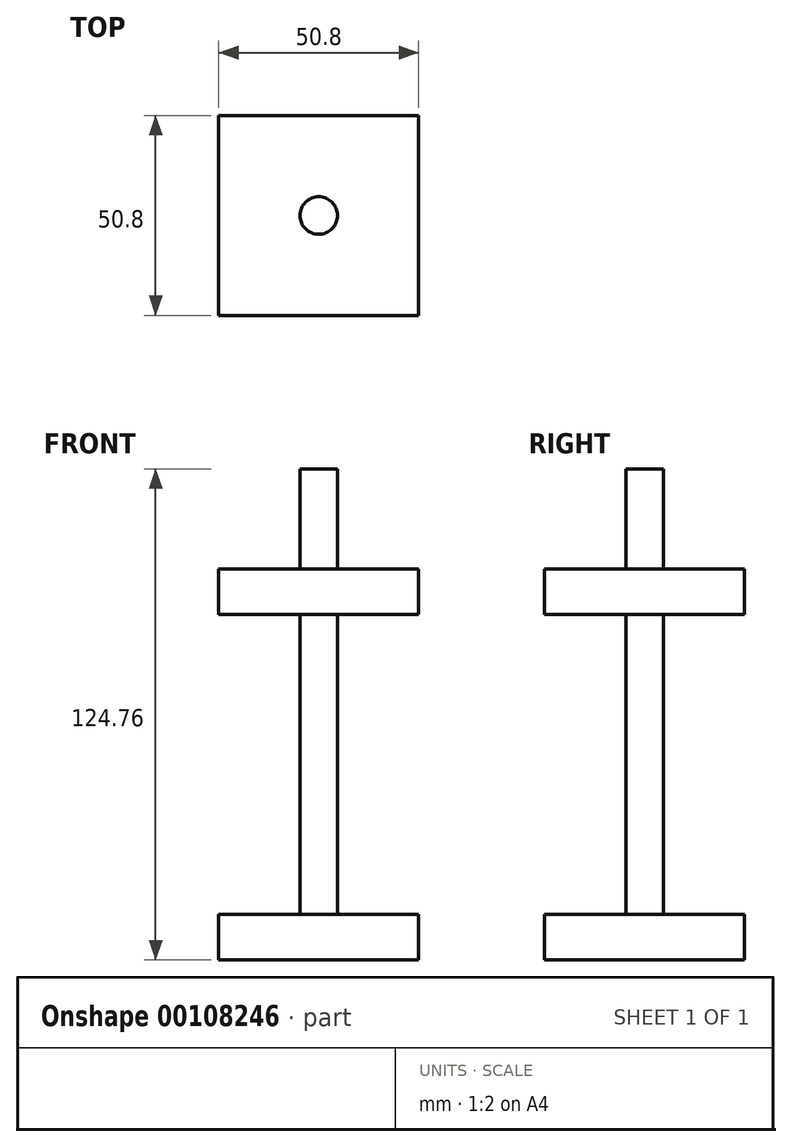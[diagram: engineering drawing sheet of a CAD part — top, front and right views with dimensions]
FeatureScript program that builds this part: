
annotation { "Feature Type Name" : "Feature", "Feature Type Description" : "" }
export const myFeature = defineFeature(function(context is Context, id is Id, definition is map)
    precondition{}
    {
        {
            var Q0;
            Q0=qCreatedBy(makeId("Top.planeOp"),FACE);
            var sketch = newSketch(context, id + "F0", { "sketchPlane" : qUnion([Q0])});
            skLineSegment(sketch, "E0.bottom", {"start": v(25.4, 25.4) * mm, "end": v(-25.4, 25.4) * mm});
            skLineSegment(sketch, "E0.top", {"start": v(25.4, -25.4) * mm, "end": v(-25.4, -25.4) * mm});
            skLineSegment(sketch, "E0.left", {"start": v(25.4, 25.4) * mm, "end": v(25.4, -25.4) * mm});
            skLineSegment(sketch, "E0.right", {"start": v(-25.4, 25.4) * mm, "end": v(-25.4, -25.4) * mm});
            skPoint(sketch, "E0.middle", {"position": v(0, 0) * mm});
            skSolve(sketch);
        }
        {
            var Q0;
            Q0=makeQuery(id+"F0.imprint","IMPRINT",FACE,{"disambiguationData":[TD([[makeQuery(id+"F0.imprint","IMPRINT",EDGE,{"derivedFrom":sQuery(id+"F0.wireOp",EDGE,"E0.bottom")}),1.0]])]});
            extrude(context, id + "F1", {"entities" : qUnion([Q0]), "depth" : 11.58 * mm});
        }
        {
            var Q0;
            Q0=makeQuery(id+"F1.opExtrude","CAP_FACE",FACE,{"disambiguationData":[OSD([sQuery(id+"F0.wireOp",EDGE,"E0.bottom"),sQuery(id+"F0.wireOp",EDGE,"E0.top"),sQuery(id+"F0.wireOp",EDGE,"E0.left"),sQuery(id+"F0.wireOp",EDGE,"E0.right")])],"isStart":false});
            var sketch = newSketch(context, id + "F2", { "sketchPlane" : qUnion([Q0])});
            skCircle(sketch, "E1", {"center": v(0, 0) * mm, "radius": 4.76 * mm});
            skSolve(sketch);
        }
        {
            var Q0;
            Q0=makeQuery(id+"F2.imprint","IMPRINT",FACE,{"disambiguationData":[TD([[makeQuery(id+"F2.imprint","IMPRINT",EDGE,{"derivedFrom":sQuery(id+"F2.wireOp",EDGE,"E1")}),1.0]])]});
            extrude(context, id + "F3", {"entities" : qUnion([Q0]), "operationType" : NewBodyOperationType.ADD, "depth" : 76.2 * mm});
        }
        {
            var Q0;
            Q0=makeQuery(id+"F3.opExtrude","CAP_FACE",FACE,{"disambiguationData":[OSD([sQuery(id+"F2.wireOp",EDGE,"E1")])],"isStart":false});
            var sketch = newSketch(context, id + "F4", { "sketchPlane" : qUnion([Q0])});
            skLineSegment(sketch, "E2.bottom", {"start": v(25.4, 25.4) * mm, "end": v(-25.4, 25.4) * mm});
            skLineSegment(sketch, "E2.top", {"start": v(25.4, -25.4) * mm, "end": v(-25.4, -25.4) * mm});
            skLineSegment(sketch, "E2.left", {"start": v(25.4, 25.4) * mm, "end": v(25.4, -25.4) * mm});
            skLineSegment(sketch, "E2.right", {"start": v(-25.4, 25.4) * mm, "end": v(-25.4, -25.4) * mm});
            skPoint(sketch, "E2.middle", {"position": v(0, 0) * mm});
            skSolve(sketch);
        }
        {
            var Q0;
            Q0=makeQuery(id+"F4.imprint","IMPRINT",FACE,{"disambiguationData":[TD([[makeQuery(id+"F4.imprint","IMPRINT",EDGE,{"derivedFrom":sQuery(id+"F4.wireOp",EDGE,"E2.bottom")}),1.0]])]});
            var Q1;
            Q1=makeQuery(id+"F4.imprint","IMPRINT",FACE,{"disambiguationData":[TD([[makeQuery(id+"F4.imprint","IMPRINT",EDGE,{"derivedFrom":makeQuery(id+"F3.opExtrude","CAP_EDGE",EDGE,{"disambiguationData":[OSD([sQuery(id+"F2.wireOp",EDGE,"E1")])],"isStart":false})}),1.0]])]});
            extrude(context, id + "F5", {"entities" : qUnion([Q0, Q1]), "operationType" : NewBodyOperationType.ADD, "depth" : 11.58 * mm});
        }
        {
            var Q0;
            Q0=makeQuery(id+"F5.opExtrude","CAP_FACE",FACE,{"disambiguationData":[OSD([sQuery(id+"F4.wireOp",EDGE,"E2.bottom"),sQuery(id+"F4.wireOp",EDGE,"E2.top"),sQuery(id+"F4.wireOp",EDGE,"E2.left"),sQuery(id+"F4.wireOp",EDGE,"E2.right")])],"isStart":false});
            var sketch = newSketch(context, id + "F6", { "sketchPlane" : qUnion([Q0])});
            skCircle(sketch, "E3", {"center": v(0, 0) * mm, "radius": 4.76 * mm});
            skSolve(sketch);
        }
        {
            var Q0;
            Q0=makeQuery(id+"F6.imprint","IMPRINT",FACE,{"disambiguationData":[TD([[makeQuery(id+"F6.imprint","IMPRINT",EDGE,{"derivedFrom":sQuery(id+"F6.wireOp",EDGE,"E3")}),1.0]])]});
            extrude(context, id + "F7", {"entities" : qUnion([Q0]), "operationType" : NewBodyOperationType.ADD, "depth" : 25.4 * mm});
        }
    });
